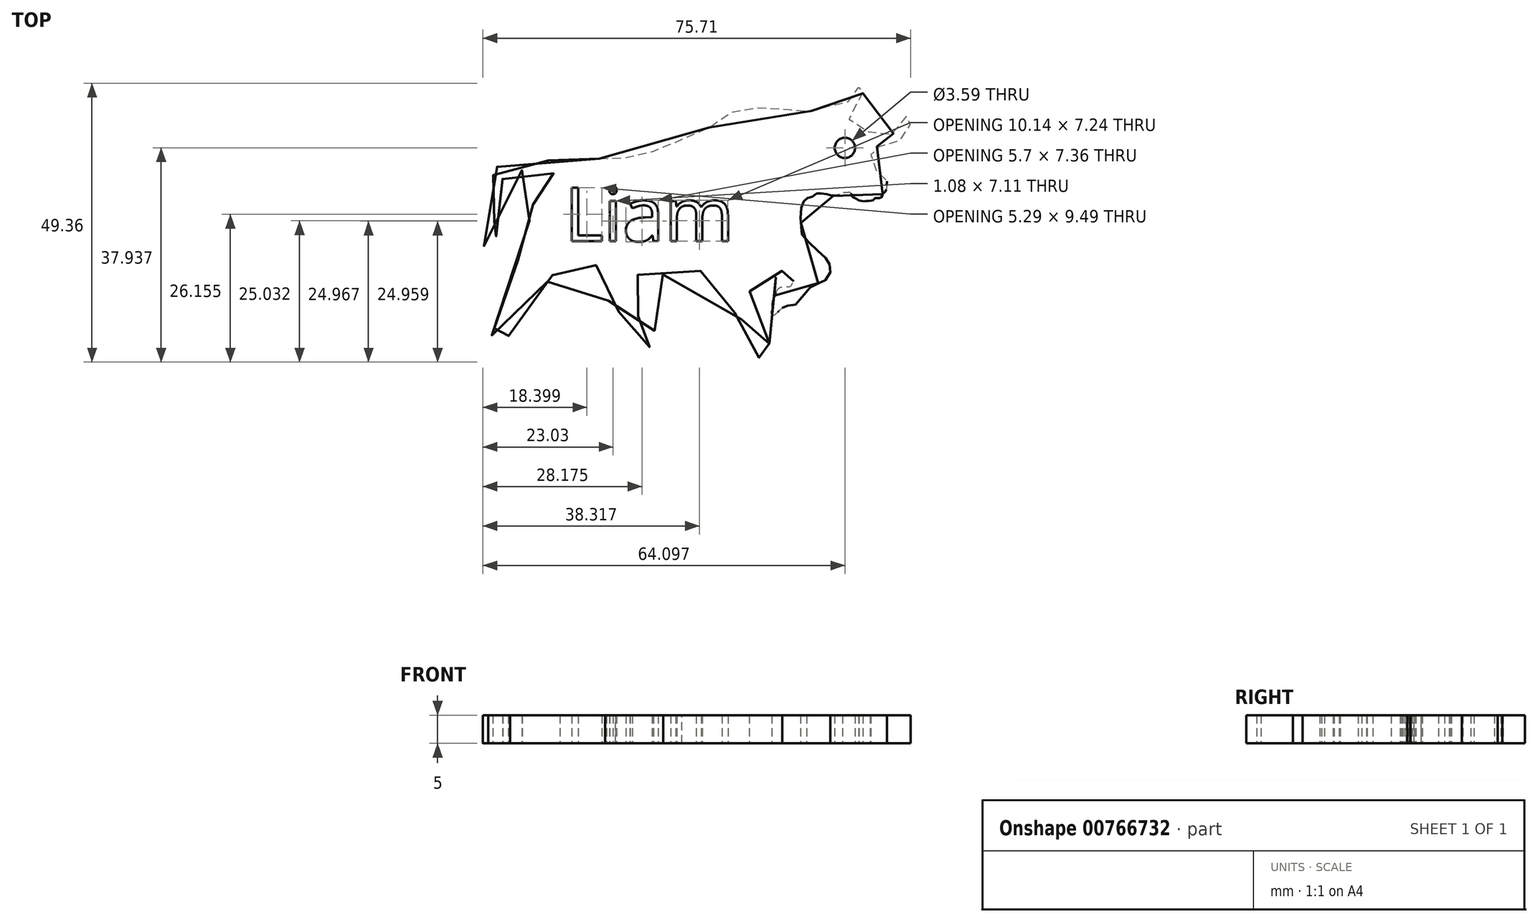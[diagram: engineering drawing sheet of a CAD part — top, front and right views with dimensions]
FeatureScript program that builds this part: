
annotation { "Feature Type Name" : "Feature", "Feature Type Description" : "" }
export const myFeature = defineFeature(function(context is Context, id is Id, definition is map)
    precondition{}
    {
        {
            var Q0;
            Q0=qCreatedBy(makeId("Top.planeOp"),FACE);
            var sketch = newSketch(context, id + "F0", { "sketchPlane" : qUnion([Q0])});
            skFitSpline(sketch, "E0", {"points": [v(-55.9, 37.07) * mm, v(-53.55, 37) * mm, v(-51.06, 37.34) * mm, v(-47.89, 38.04) * mm, v(-44.92, 38.8) * mm, v(-41.88, 40.25) * mm, v(-38, 41.83) * mm, v(-35.25, 43.42) * mm, v(-32.97, 45.15) * mm, v(-30.27, 45.84) * mm, v(-27.92, 46.12) * mm, v(-23.99, 45.98) * mm, v(-20.19, 45.36) * mm, v(-18.53, 45.08) * mm, v(-18.25, 45.91) * mm, v(-17.08, 46.4) * mm, v(-14.6, 46.46) * mm, v(-13.35, 46.46) * mm, v(-12.1, 47.02) * mm, v(-11.28, 47.64) * mm, v(-10.45, 48.74) * mm, v(-9.96, 49.85) * mm, v(-9.96, 50.4) * mm, v(-9.55, 50.2) * mm, v(-9.27, 49.16) * mm, v(-9.34, 47.57) * mm, v(-10.58, 45.84) * mm, v(-12.31, 44.74) * mm, v(-12.86, 44.67) * mm, v(-11.41, 43.9) * mm, v(-9.76, 42.66) * mm, v(-8.03, 41.77) * mm, v(-6.03, 41.49) * mm, v(-3.95, 41.49) * mm, v(-2.5, 42.94) * mm, v(-1.4, 44.8) * mm, v(-0.98, 45.56) * mm, v(-0.85, 43.67) * mm, v(-1.25, 42.1) * mm, v(-2.18, 40.8) * mm, v(-3.5, 39.83) * mm, v(-5.26, 39.37) * mm, v(-6.77, 39.22) * mm, v(-7.9, 39.34) * mm, v(-7.85, 38.3) * mm, v(-7.82, 37.28) * mm, v(-7.2, 36.14) * mm, v(-6.98, 35.19) * mm, v(-6.4, 34.34) * mm, v(-5.64, 33.53) * mm, v(-5, 33.15) * mm, v(-5, 32.86) * mm, v(-5.12, 31.7) * mm, v(-5.47, 31.06) * mm, v(-5.7, 31) * mm, v(-5.81, 30.63) * mm, v(-6.16, 30.13) * mm, v(-7.12, 30.07) * mm, v(-7.38, 29.78) * mm, v(-8.08, 29.64) * mm, v(-9.13, 29.55) * mm, v(-9.94, 29.73) * mm, v(-10.6, 30.07) * mm, v(-11.25, 30.54) * mm, v(-11.42, 31.03) * mm, v(-12.52, 31.03) * mm, v(-13.4, 30.98) * mm, v(-13.63, 30.57) * mm, v(-14.5, 30.48) * mm, v(-14.96, 30.66) * mm, v(-15.4, 30.8) * mm, v(-16.18, 30.83) * mm, v(-16.62, 30.95) * mm, v(-17, 31.03) * mm, v(-17.35, 30.98) * mm, v(-17.75, 30.54) * mm, v(-18.13, 30.37) * mm, v(-18.48, 30.25) * mm, v(-19.06, 30.13) * mm, v(-19.47, 30.05) * mm, v(-19.76, 29.4) * mm, v(-20.1, 28.7) * mm, v(-20.28, 27.14) * mm, v(-20.2, 25.37) * mm, v(-20.16, 24.76) * mm, v(-19.9, 23.33) * mm, v(-18.38, 21.91) * mm, v(-16.77, 20.25) * mm, v(-15.4, 18.98) * mm, v(-15.15, 18.2) * mm, v(-15, 17.13) * mm, v(-15.74, 15.8) * mm, v(-16.47, 15.17) * mm, v(-17.55, 14.98) * mm, v(-19.3, 13.56) * mm, v(-20.82, 11.6) * mm, v(-21.7, 11.02) * mm, v(-22.87, 11.07) * mm, v(-23.26, 10.88) * mm, v(-24.2, 10.05) * mm, v(-25.22, 9.31) * mm, v(-25.31, 10.63) * mm, v(-25.17, 11.75) * mm, v(-24.73, 13.27) * mm, v(-23.7, 14.34) * mm, v(-22.04, 14.5) * mm, v(-21.65, 15.22) * mm, v(-19.9, 16.2) * mm, v(-19.26, 16.83) * mm, v(-20.58, 17.18) * mm, v(-21.65, 17.47) * mm, v(-22.63, 17.67) * mm, v(-23.75, 17.08) * mm, v(-25.02, 15.56) * mm, v(-26, 14.2) * mm, v(-27.51, 14.34) * mm, v(-29.27, 14.78) * mm, v(-28.98, 12.15) * mm, v(-28.73, 10.2) * mm, v(-28.34, 8.82) * mm, v(-27.12, 6.43) * mm, v(-25.46, 3.99) * mm, v(-23.95, 2.91) * mm, v(-23.56, 1.89) * mm, v(-24.34, 1.3) * mm, v(-25.5, 1.06) * mm, v(-27.66, 1.89) * mm, v(-28.93, 4.04) * mm, v(-29.66, 6.63) * mm, v(-30.2, 8.1) * mm, v(-31.32, 9.07) * mm, v(-33.08, 11.75) * mm, v(-34, 14.25) * mm, v(-35.18, 15.9) * mm, v(-36.7, 16.69) * mm, v(-39.58, 17.52) * mm, v(-42.21, 16.93) * mm, v(-45.05, 16.54) * mm, v(-48.9, 16.5) * mm, v(-50.23, 16.5) * mm, v(-50.52, 15.13) * mm, v(-50.52, 13.61) * mm, v(-50.18, 10.88) * mm, v(-48.66, 8.82) * mm, v(-47.4, 7.5) * mm, v(-45.98, 6.48) * mm, v(-44.6, 4.72) * mm, v(-46.32, 3.9) * mm, v(-48.37, 3.84) * mm, v(-49.25, 5.36) * mm, v(-50.08, 6.82) * mm, v(-51.06, 8.58) * mm, v(-52.77, 10.2) * mm, v(-54.33, 11.95) * mm, v(-54.91, 13.46) * mm, v(-54.77, 16.5) * mm, v(-56.53, 18.3) * mm, v(-57.9, 20.7) * mm, v(-59.8, 20.45) * mm, v(-62.05, 19.18) * mm, v(-65.02, 15.44) * mm, v(-69.12, 11.72) * mm, v(-71.66, 8.99) * mm, v(-71.85, 4.69) * mm, v(-71.85, 3.52) * mm, v(-74.4, 2.93) * mm, v(-75.57, 3.71) * mm, v(-74.6, 6.84) * mm, v(-73.42, 13.68) * mm, v(-71.46, 16.02) * mm, v(-70.6, 18.56) * mm, v(-69.63, 20.43) * mm, v(-69.57, 22.57) * mm, v(-68.46, 25.54) * mm, v(-67.77, 28.44) * mm, v(-67.29, 30.65) * mm, v(-66.94, 32.03) * mm, v(-64.25, 33.62) * mm, v(-62.93, 34.17) * mm, v(-64.32, 34.52) * mm, v(-65.97, 34.8) * mm, v(-69.43, 35.07) * mm, v(-72.12, 34.38) * mm, v(-73.02, 33.83) * mm, v(-72.47, 31.27) * mm, v(-71.98, 27.82) * mm, v(-73.5, 25.12) * mm, v(-74.2, 23.33) * mm, v(-75.78, 21.53) * mm, v(-76.34, 21.6) * mm, v(-76.54, 22.57) * mm, v(-76.34, 23.67) * mm, v(-75.3, 25.54) * mm, v(-73.3, 26.64) * mm, v(-73.09, 28.65) * mm, v(-73.85, 30.51) * mm, v(-74.54, 32.45) * mm, v(-74.6, 34.8) * mm, v(-73.16, 36.25) * mm, v(-70.53, 36.8) * mm, v(-66.73, 36.94) * mm, v(-62.66, 36.38) * mm, v(-60.38, 36.31) * mm, v(-59.55, 37.21) * mm, v(-56.65, 37.21) * mm, v(-55.9, 37.07) * mm]});
            skText(sketch, "E1", { "text": "Liam", "fontName": "OpenSans-Regular.ttf"});
            skCircle(sketch, "E2", {"center": v(-12.44, 39) * mm, "radius": 1.8 * mm});
            const initialGuessF0  = {"E1": [-0.06209, 0.02247, 1, 0, 0.00957]};
            skSetInitialGuess(sketch, initialGuessF0);
            skSolve(sketch);
        }
        {
            var Q0;
            Q0 = qSketchRegion(id + "F0", true);
            extrude(context, id + "F1", {"entities" : qUnion([Q0]), "depth" : 5 * mm, "offsetDistance" : 25.4 * mm});
        }
    });
